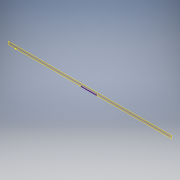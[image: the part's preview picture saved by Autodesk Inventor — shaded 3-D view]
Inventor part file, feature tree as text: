
AUTODESK INVENTOR PART (.ipt)
format: ipt  version: 2016 (Build 200138000, 138)  size: 114,176 bytes
history: native  units: in
note: dims shown in document units (in); Inventor stores cm internally (conversion verified against a paired STEP export)
features: reference x2, plane x1, extrude x1, sketch x1
ambient origin geometry x8: Origin, YZ Plane, XZ Plane, XY Plane, X Axis, Y Axis, Z Axis, Center Point
bodies: Solid1 (feature_tree)
feature tree (5):
  plane  "Work Plane1"
  extrude  "Extrusion1"  Depth=2.5in
  sketch  "Sketch1"  dims[d0=10.544in d1=2.5in d2=10.25in d3=0.5in d5=0.175in d7=0.175in d8=0.7874in d10=1.0in d11=0.3937in d13=1.0in d15=0.24in d16=0.0in]
  reference  "Reference1"
  reference  "Reference2"
